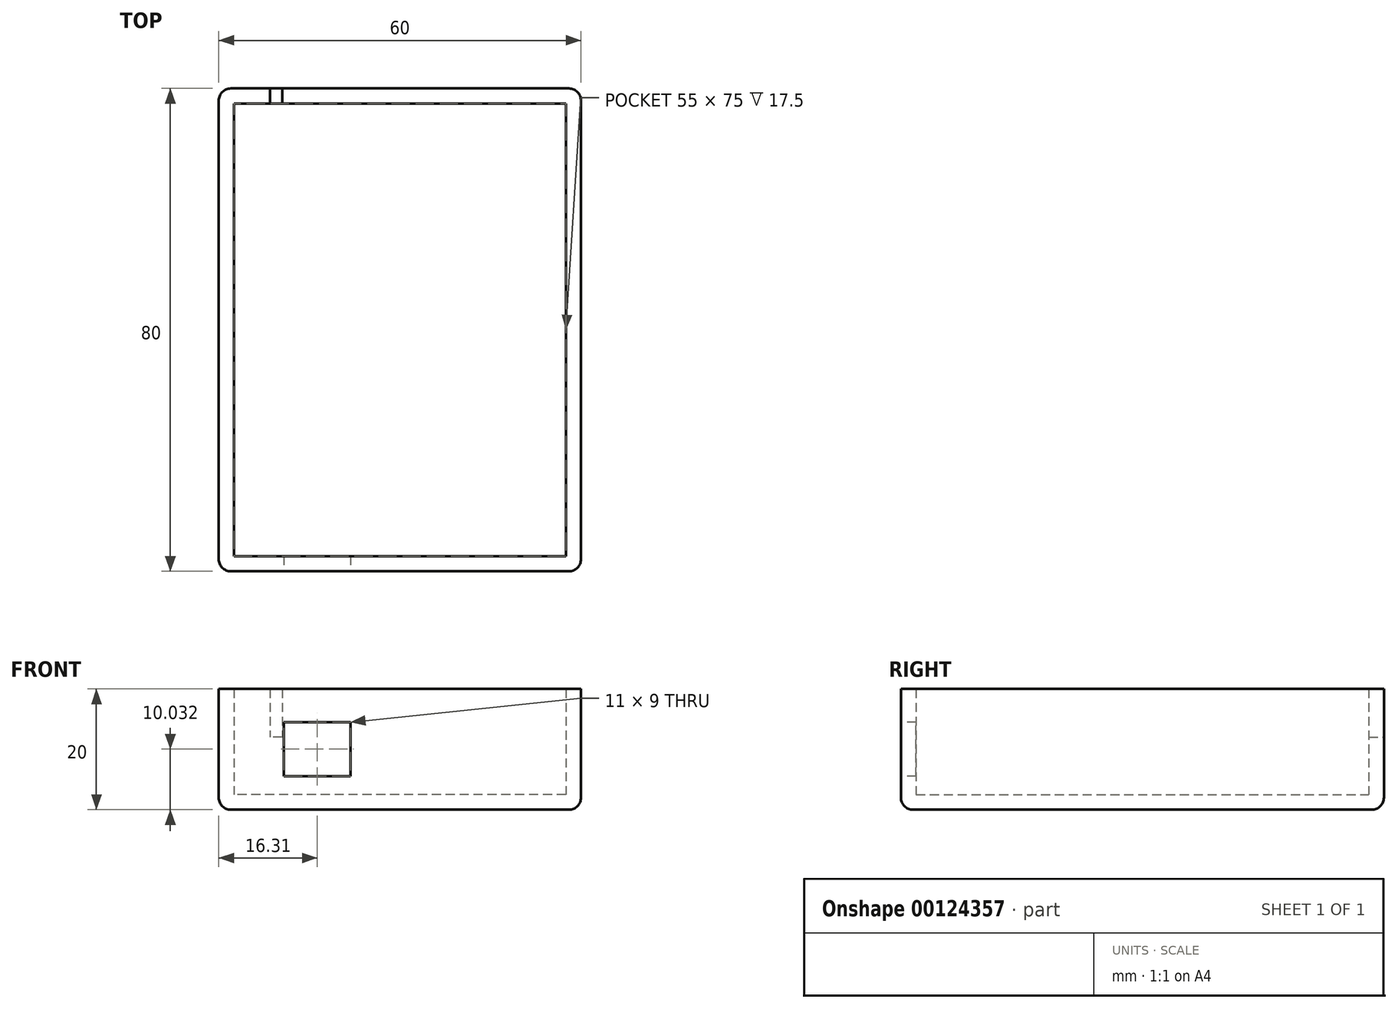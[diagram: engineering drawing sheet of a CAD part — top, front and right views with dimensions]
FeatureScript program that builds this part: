
annotation { "Feature Type Name" : "Feature", "Feature Type Description" : "" }
export const myFeature = defineFeature(function(context is Context, id is Id, definition is map)
    precondition{}
    {
        {
            var Q0;
            Q0=qCreatedBy(makeId("Top.planeOp"),FACE);
            var sketch = newSketch(context, id + "F0", { "sketchPlane" : qUnion([Q0])});
            skLineSegment(sketch, "E0", {"start": v(-28.64, 57.23) * mm, "end": v(31.36, 57.23) * mm});
            skLineSegment(sketch, "E1", {"start": v(31.36, 57.23) * mm, "end": v(31.36, -22.77) * mm});
            skLineSegment(sketch, "E2", {"start": v(31.36, -22.77) * mm, "end": v(-28.64, -22.77) * mm});
            skLineSegment(sketch, "E3", {"start": v(-28.64, -22.77) * mm, "end": v(-28.64, 57.23) * mm});
            skSolve(sketch);
        }
        {
            var Q0;
            Q0 = qSketchRegion(id + "F0", true);
            extrude(context, id + "F1", {"entities" : qUnion([Q0]), "depth" : 20 * mm});
        }
        {
            var Q0;
            Q0=makeQuery(id+"F1.opExtrude","CAP_FACE",FACE,{"disambiguationData":[OSD([sQuery(id+"F0.wireOp",EDGE,"E0"),sQuery(id+"F0.wireOp",EDGE,"E1"),sQuery(id+"F0.wireOp",EDGE,"E2"),sQuery(id+"F0.wireOp",EDGE,"E3")])],"isStart":false});
            shell(context, id + "F2", {"entities" : qUnion([Q0]), "thickness" : 2.5 * mm});
        }
        {
            var Q0;
            Q0=makeQuery(id+"F1.opExtrude","SWEPT_FACE",FACE,{"disambiguationData":[OSD([sQuery(id+"F0.wireOp",EDGE,"E2")])]});
            var sketch = newSketch(context, id + "F3", { "sketchPlane" : qUnion([Q0])});
            skLineSegment(sketch, "E4.bottom", {"start": v(-17.83, 5.53) * mm, "end": v(-6.83, 5.53) * mm});
            skLineSegment(sketch, "E4.top", {"start": v(-17.83, 14.53) * mm, "end": v(-6.83, 14.53) * mm});
            skLineSegment(sketch, "E4.left", {"start": v(-17.83, 5.53) * mm, "end": v(-17.83, 14.53) * mm});
            skLineSegment(sketch, "E4.right", {"start": v(-6.83, 5.53) * mm, "end": v(-6.83, 14.53) * mm});
            skSolve(sketch);
        }
        {
            var Q0;
            Q0 = qSketchRegion(id + "F3", true);
            extrude(context, id + "F4", {"entities" : qUnion([Q0]), "operationType" : NewBodyOperationType.REMOVE, "oppositeDirection" : true, "depth" : 10 * mm});
        }
        {
            var Q0;
            Q0=makeQuery(id+"F1.opExtrude","SWEPT_FACE",FACE,{"disambiguationData":[OSD([sQuery(id+"F0.wireOp",EDGE,"E0")])]});
            var sketch = newSketch(context, id + "F5", { "sketchPlane" : qUnion([Q0])});
            skLineSegment(sketch, "E5.bottom", {"start": v(18.12, 20) * mm, "end": v(20.12, 20) * mm});
            skLineSegment(sketch, "E5.top", {"start": v(18.12, 12) * mm, "end": v(20.12, 12) * mm});
            skLineSegment(sketch, "E5.left", {"start": v(18.12, 20) * mm, "end": v(18.12, 12) * mm});
            skLineSegment(sketch, "E5.right", {"start": v(20.12, 20) * mm, "end": v(20.12, 12) * mm});
            skSolve(sketch);
        }
        {
            var Q0;
            Q0 = qSketchRegion(id + "F5", true);
            extrude(context, id + "F6", {"entities" : qUnion([Q0]), "operationType" : NewBodyOperationType.REMOVE, "oppositeDirection" : true, "depth" : 25 * mm});
        }
        {
            var Q0;
            Q0=makeQuery(id+"F1.opExtrude","SWEPT_EDGE",EDGE,{"disambiguationData":[OSD([sQuery(id+"F0.wireOp",EDGE,"E1"),sQuery(id+"F0.wireOp",EDGE,"E2")])]});
            var Q1;
            Q1=makeQuery(id+"F1.opExtrude","SWEPT_EDGE",EDGE,{"disambiguationData":[OSD([sQuery(id+"F0.wireOp",EDGE,"E0"),sQuery(id+"F0.wireOp",EDGE,"E1")])]});
            var Q2;
            Q2=makeQuery(id+"F1.opExtrude","SWEPT_EDGE",EDGE,{"disambiguationData":[OSD([sQuery(id+"F0.wireOp",EDGE,"E0"),sQuery(id+"F0.wireOp",EDGE,"E3")])]});
            var Q3;
            Q3=makeQuery(id+"F1.opExtrude","SWEPT_EDGE",EDGE,{"disambiguationData":[OSD([sQuery(id+"F0.wireOp",EDGE,"E2"),sQuery(id+"F0.wireOp",EDGE,"E3")])]});
            fillet(context, id + "F7", {"entities" : qUnion([Q0, Q1, Q2, Q3]), "radius" : 2 * mm, "tangentPropagation" : true, "allowEdgeOverflow" : false});
        }
        {
            var Q0;
            Q0=makeQuery(id+"F1.opExtrude","CAP_FACE",FACE,{"disambiguationData":[OSD([sQuery(id+"F0.wireOp",EDGE,"E0"),sQuery(id+"F0.wireOp",EDGE,"E1"),sQuery(id+"F0.wireOp",EDGE,"E2"),sQuery(id+"F0.wireOp",EDGE,"E3")])],"isStart":true});
            fillet(context, id + "F8", {"entities" : qUnion([Q0]), "radius" : 2 * mm, "tangentPropagation" : true, "allowEdgeOverflow" : false});
        }
    });
